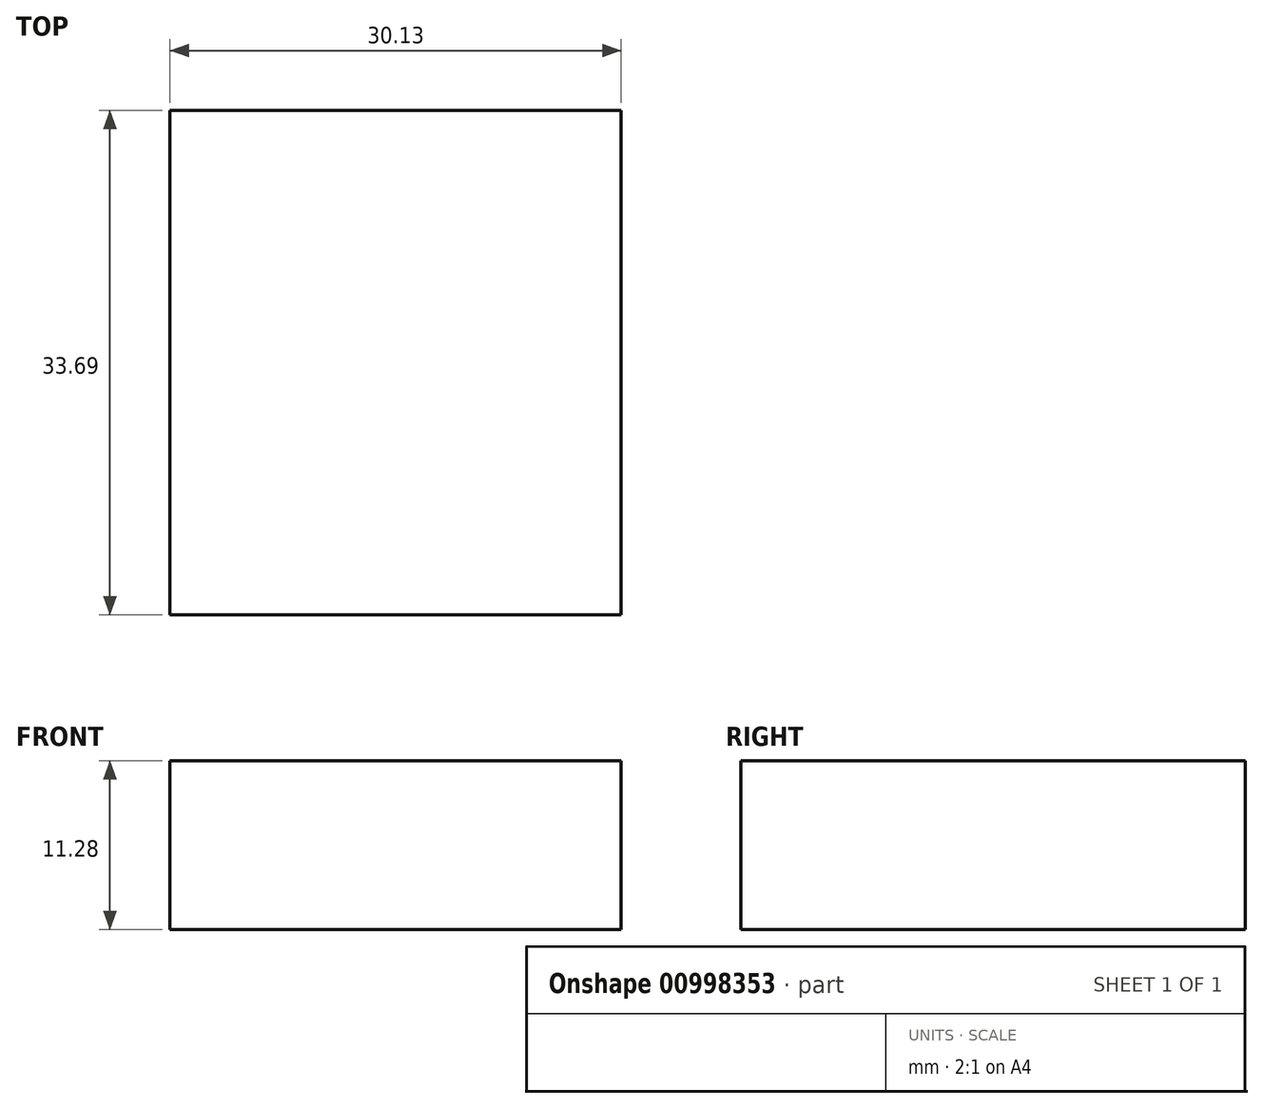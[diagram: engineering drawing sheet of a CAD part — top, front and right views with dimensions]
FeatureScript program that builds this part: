
annotation { "Feature Type Name" : "Feature", "Feature Type Description" : "" }
export const myFeature = defineFeature(function(context is Context, id is Id, definition is map)
    precondition{}
    {
        {
            var Q0;
            Q0=qCreatedBy(makeId("Top.planeOp"),FACE);
            var sketch = newSketch(context, id + "F0", { "sketchPlane" : qUnion([Q0])});
            skLineSegment(sketch, "E0", {"start": v(0, 0) * mm, "end": v(0, -33.69) * mm});
            skLineSegment(sketch, "E1", {"start": v(0, -33.69) * mm, "end": v(30.13, -33.69) * mm});
            skLineSegment(sketch, "E2", {"start": v(30.13, -33.69) * mm, "end": v(30.13, 0) * mm});
            skLineSegment(sketch, "E3", {"start": v(30.13, 0) * mm, "end": v(0, 0) * mm});
            skSolve(sketch);
        }
        {
            var Q0;
            Q0=makeQuery(id+"F0.imprint","IMPRINT",FACE,{"disambiguationData":[TD([[makeQuery(id+"F0.imprint","IMPRINT",EDGE,{"derivedFrom":sQuery(id+"F0.wireOp",EDGE,"E0")}),1.0]])]});
            extrude(context, id + "F1", {"entities" : qUnion([Q0]), "depth" : 11.28 * mm, "offsetDistance" : 25 * mm});
        }
    });
